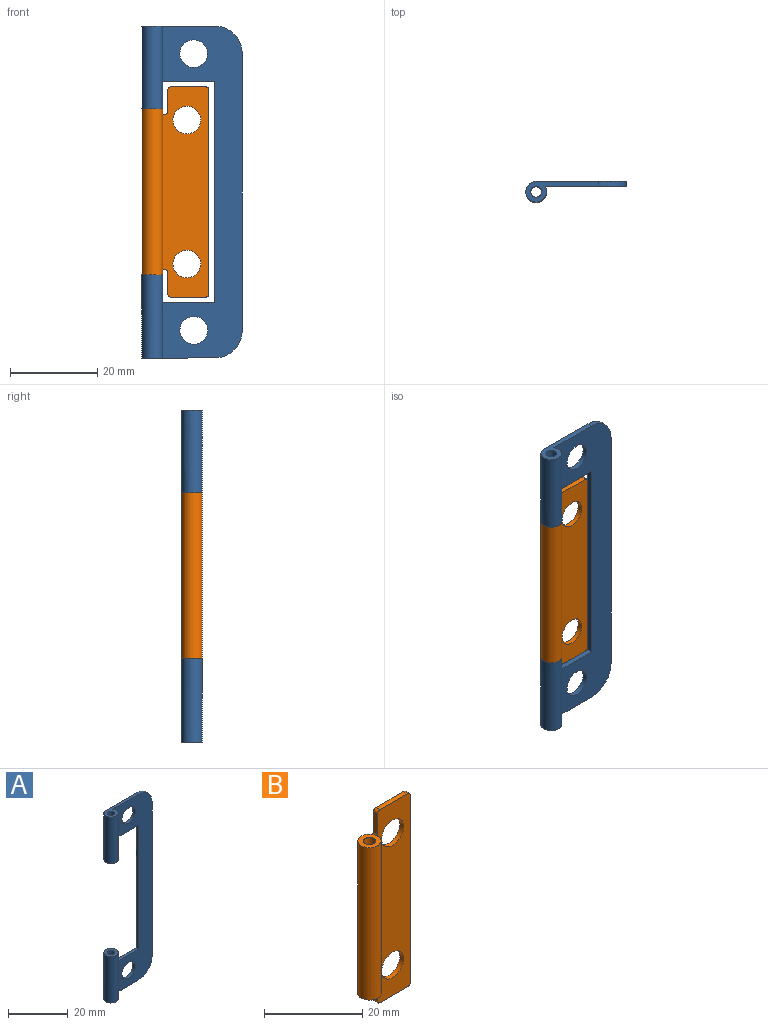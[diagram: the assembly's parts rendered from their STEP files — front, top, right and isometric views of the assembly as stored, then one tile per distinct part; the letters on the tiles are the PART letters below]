
ASSEMBLY  parts=2 mates=1
PART A: 18 faces, bbox 23x4.8x76.2 mm
  f0: plane 76.2x18.6mm, normal (0,-1,0), area 714.5mm2, adj f1,f2,f3,f4,f5,f6,f7,f8
  f1: plane 16.67x4.76mm, normal (0,0,-1), area 27.7mm2, adj f0,f2,f11,f15,f16
  f2: cylinder r=6.35mm len=6.35mm, axis (0,1,0), area 11.4mm2, adj f0,f1,f3,f11
  f3: plane 63.5x1.14mm, normal (1,0,0), area 72.6mm2, adj f0,f2,f4,f11
  f4: cylinder r=6.35mm len=6.35mm, axis (0,1,0), area 11.4mm2, adj f0,f3,f5,f11
  f5: plane 16.67x4.76mm, normal (0,0,1), area 27.7mm2, adj f0,f4,f11,f12,f13
  f6: plane 14.29x1.14mm, normal (0,0,-1), area 14.7mm2, adj f0,f7,f11,f12
  f7: plane 50.8x1.14mm, normal (-1,0,0), area 58.1mm2, adj f0,f6,f8,f11
  f8: plane 14.29x1.14mm, normal (0,0,1), area 14.7mm2, adj f0,f7,f11,f15
  f9: cylinder r=3.17mm len=6.35mm, axis (0,1,0), area 22.8mm2, adj f0,f11
  f10: cylinder r=3.17mm len=6.35mm, axis (0,1,0), area 22.8mm2, adj f0,f11
  f11: plane 76.2x20.64mm, normal (0,1,0), area 766.1mm2, adj f1,f2,f3,f4,f5,f6,f7,f8
  f12: cylinder r=2.38mm len=19.05mm, axis (0,0,1), area 254.1mm2, adj f0,f5,f6,f11,f14
  f13: cylinder r=1.24mm len=19.05mm, axis (0,0,1), area 148.2mm2, adj f5,f14
  f14: plane 4.76x4.76mm, normal (0,0,-1), area 13mm2, adj f12,f13
  f15: cylinder r=2.38mm len=19.05mm, axis (0,0,-1), area 254.1mm2, adj f0,f1,f8,f11,f17
  f16: cylinder r=1.24mm len=19.05mm, axis (0,0,-1), area 148.2mm2, adj f1,f17
  f17: plane 4.76x4.76mm, normal (0,0,1), area 13mm2, adj f15,f16
PART B: 21 faces, bbox 15.4x4.8x48.3 mm
  f0: cylinder r=2.38mm len=38.1mm, axis (0,0,1), area 483.3mm2, adj f2,f3,f15,f17,f19,f20
  f1: cylinder r=1.24mm len=38.1mm, axis (0,0,1), area 296.4mm2, adj f2,f3
  f2: plane 4.76x4.76mm, normal (0,0,-1), area 13mm2, adj f0,f1
  f3: plane 4.76x4.76mm, normal (0,0,1), area 13mm2, adj f0,f1
  f4: cylinder r=0.76mm len=1.14mm, axis (0,1,0), area 1.4mm2, adj f5,f17,f19,f20
  f5: plane 4.83x1.14mm, normal (-1,0,0), area 5.5mm2, adj f4,f6,f19,f20
  f6: cylinder r=0.76mm len=1.14mm, axis (0,1,0), area 1.4mm2, adj f5,f7,f19,f20
  f7: plane 7.94x1.14mm, normal (0,0,-1), area 9.1mm2, adj f6,f8,f19,f20
  f8: cylinder r=0.76mm len=1.14mm, axis (0,1,0), area 1.4mm2, adj f7,f9,f19,f20
  f9: plane 46.74x1.14mm, normal (1,0,0), area 53.4mm2, adj f8,f10,f19,f20
  f10: cylinder r=0.76mm len=1.14mm, axis (0,1,0), area 1.4mm2, adj f9,f11,f19,f20
  f11: plane 7.94x1.14mm, normal (0,0,1), area 9.1mm2, adj f10,f12,f19,f20
  f12: cylinder r=0.76mm len=1.14mm, axis (0,1,0), area 1.4mm2, adj f11,f13,f19,f20
  f13: plane 4.83x1.14mm, normal (-1,0,0), area 5.5mm2, adj f12,f14,f19,f20
  f14: cylinder r=0.76mm len=1.14mm, axis (0,1,0), area 1.4mm2, adj f13,f15,f19,f20
  f15: plane 2.79x1.14mm, normal (0,0,1), area 1.5mm2, adj f0,f14,f19,f20
  f16: cylinder r=3.17mm len=6.35mm, axis (0,1,0), area 22.8mm2, adj f19,f20
  f17: plane 2.79x1.14mm, normal (0,0,-1), area 1.5mm2, adj f0,f4,f19,f20
  f18: cylinder r=3.17mm len=6.35mm, axis (0,1,0), area 22.8mm2, adj f19,f20
  f19: plane 48.26x10.98mm, normal (0,-1,0), area 447.1mm2, adj f0,f4,f5,f6,f7,f8,f9,f10
  f20: plane 48.26x13.02mm, normal (0,1,0), area 519.5mm2, adj f0,f4,f5,f6,f7,f8,f9,f10
PLACE A at identity fixed
PLACE B at identity
MATE revolute A.f12 <-> B.f0  axis (0,0,-1) through (0,-1.81,57.15)mm
